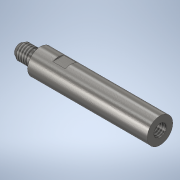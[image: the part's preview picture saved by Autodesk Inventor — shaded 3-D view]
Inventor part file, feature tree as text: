
AUTODESK INVENTOR PART (.ipt)
format: ipt  version: 2020 (Build 240168000, 168)  size: 167,936 bytes
history: native  units: mm
features: sketch x4, thread x3, extrude x2, chamfer x2, revolve x1, hole x1, fillet x1, projected_geometry x1
ambient origin geometry x8: Origin, YZ Plane, XZ Plane, XY Plane, X Axis, Y Axis, Z Axis, Center Point
bodies: Volumenkörper1 (feature_tree)
feature tree (15):
  revolve  "Umdrehung1"
  hole  "Bohrung1"  [1 undecoded]
  extrude  "Extrusion1"  TaperAngle=90.0deg  [1 undecoded]
  chamfer  "Chamfer6"  Distance=10.0mm
  chamfer  "Chamfer7"  Distance=4.4mm
  fillet  "Fillet3"  Radius=1.1mm
  thread  "Thread3"  [1 undecoded]
  extrude  "Extrusion2"  Depth=35.0mm TaperAngle=30.0deg
  thread  "Thread2"  [1 undecoded]
  thread  "Gewinde1"  [1 undecoded]
  sketch  "Skizze1"  dims[d1=6.0mm d2=10.0mm]
  sketch  "Skizze2"  dims[d3=8.0mm d4=90.0deg]
  sketch  "Sketch3"  dims[d5=4.917mm d6=9.0mm d7=4.0mm d8=2.0mm d9=90.0deg d10=13.0mm d11=20.594885mm d12=10.0mm d13=0.0mm]
  sketch  "Sketch4"  dims[d17=47.0mm d21=4.4mm d22=1.1mm d23=0.0mm d28=5.286mm d29=0.0mm d37=1.4mm d38=0.8mm d39=30.0deg d40=1.4mm d41=0.8mm d42=30.0deg d43=0.6mm d44=4.1mm d45=0.0mm d46=5.0mm d47=0.5mm d48=5.0mm d49=0.5mm d50=35.0mm d51=35.0mm d52=1.561mm d53=0.0mm]
  projected_geometry  "Projected Loop1"
note: 5 required parameter values undecoded (feature->parameter linkage not recoverable at this tier; creation-order binding heuristic only, values carry confidence <= 0.55)
